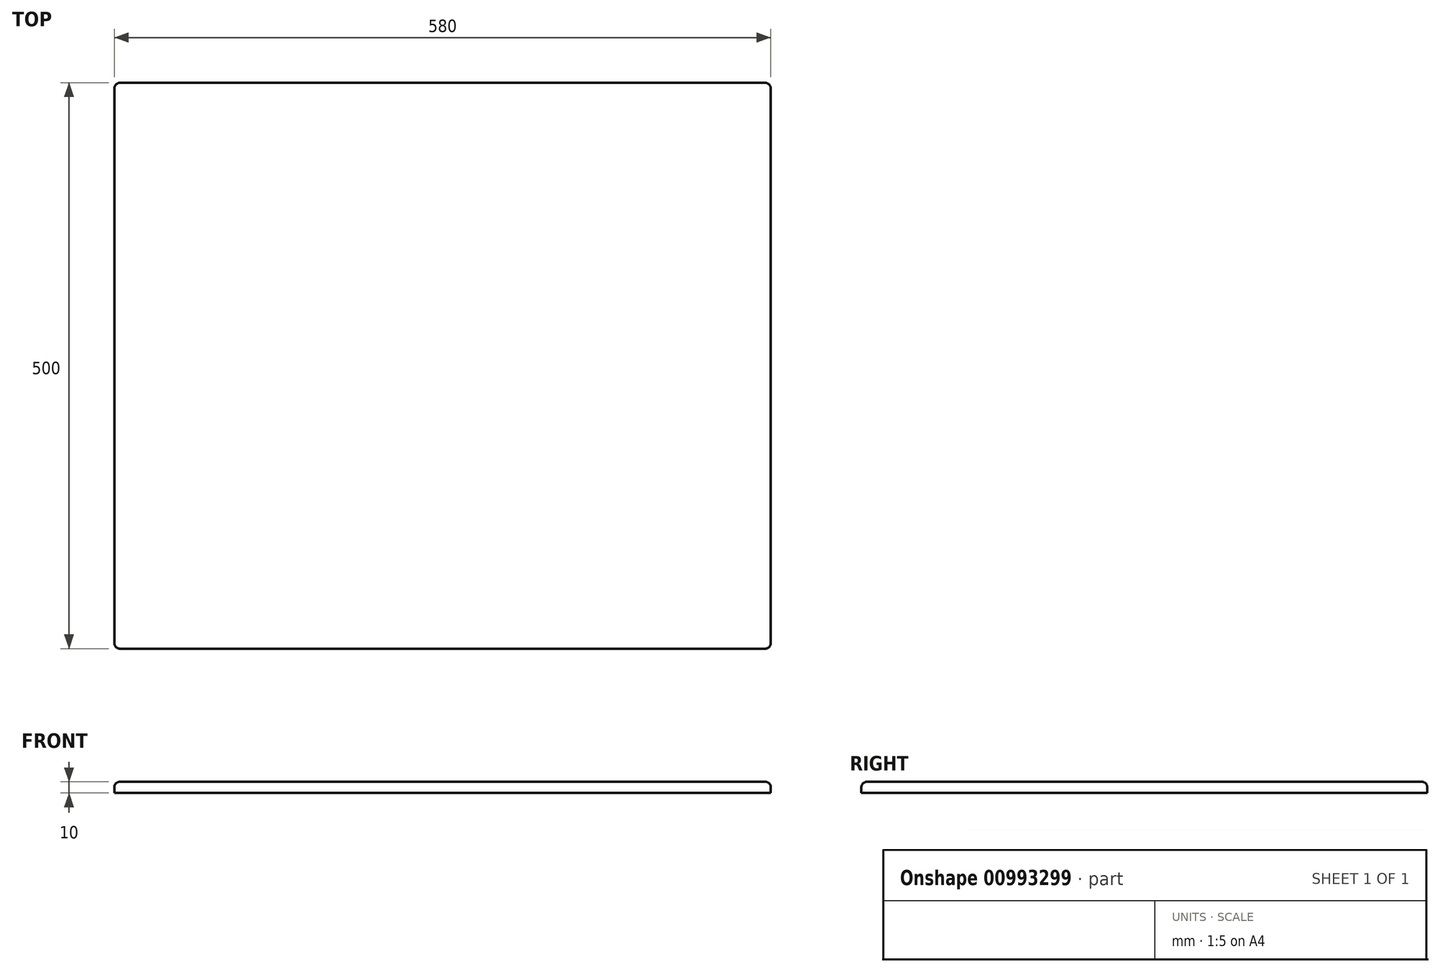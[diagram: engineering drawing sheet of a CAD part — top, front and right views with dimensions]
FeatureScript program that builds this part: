
annotation { "Feature Type Name" : "Feature", "Feature Type Description" : "" }
export const myFeature = defineFeature(function(context is Context, id is Id, definition is map)
    precondition{}
    {
        {
            var Q0;
            Q0=qCreatedBy(makeId("Top.planeOp"),FACE);
            var sketch = newSketch(context, id + "F0", { "sketchPlane" : qUnion([Q0])});
            skLineSegment(sketch, "E0.bottom", {"start": v(0, 0) * mm, "end": v(580, 0) * mm});
            skLineSegment(sketch, "E0.top", {"start": v(0, 500) * mm, "end": v(580, 500) * mm});
            skLineSegment(sketch, "E0.left", {"start": v(0, 0) * mm, "end": v(0, 500) * mm});
            skLineSegment(sketch, "E0.right", {"start": v(580, 0) * mm, "end": v(580, 500) * mm});
            skSolve(sketch);
        }
        {
            var Q0;
            Q0 = qSketchRegion(id + "F0", true);
            extrude(context, id + "F1", {"entities" : qUnion([Q0]), "depth" : 10 * mm, "offsetDistance" : 25 * mm});
        }
        {
            var Q0;
            Q0=makeQuery(id+"F1.opExtrude","CAP_FACE",FACE,{"disambiguationData":[OSD([sQuery(id+"F0.wireOp",EDGE,"E0.bottom"),sQuery(id+"F0.wireOp",EDGE,"E0.top"),sQuery(id+"F0.wireOp",EDGE,"E0.left"),sQuery(id+"F0.wireOp",EDGE,"E0.right")])],"isStart":false});
            var Q1;
            Q1=makeQuery(id+"F1.opExtrude","SWEPT_EDGE",EDGE,{"disambiguationData":[OSD([sQuery(id+"F0.wireOp",EDGE,"E0.bottom"),sQuery(id+"F0.wireOp",EDGE,"E0.left")])]});
            var Q2;
            Q2=makeQuery(id+"F1.opExtrude","SWEPT_EDGE",EDGE,{"disambiguationData":[OSD([sQuery(id+"F0.wireOp",EDGE,"E0.bottom"),sQuery(id+"F0.wireOp",EDGE,"E0.right")])]});
            var Q3;
            Q3=makeQuery(id+"F1.opExtrude","SWEPT_EDGE",EDGE,{"disambiguationData":[OSD([sQuery(id+"F0.wireOp",EDGE,"E0.top"),sQuery(id+"F0.wireOp",EDGE,"E0.right")])]});
            var Q4;
            Q4=makeQuery(id+"F1.opExtrude","SWEPT_EDGE",EDGE,{"disambiguationData":[OSD([sQuery(id+"F0.wireOp",EDGE,"E0.top"),sQuery(id+"F0.wireOp",EDGE,"E0.left")])]});
            fillet(context, id + "F2", {"entities" : qUnion([Q0, Q1, Q2, Q3, Q4]), "radius" : 5 * mm, "tangentPropagation" : true, "allowEdgeOverflow" : false});
        }
    });
